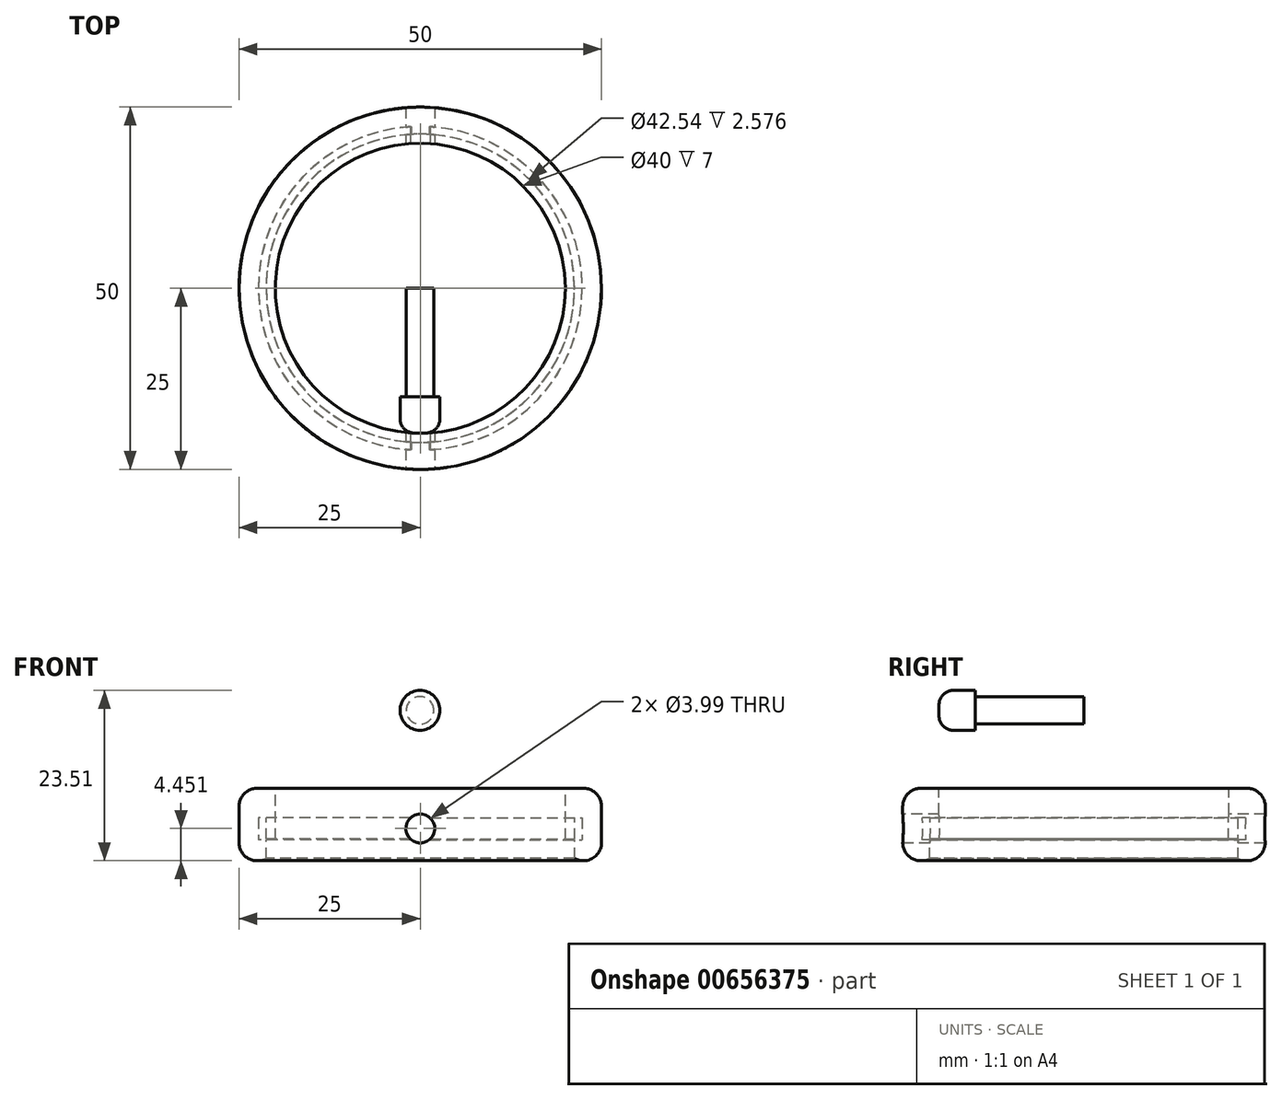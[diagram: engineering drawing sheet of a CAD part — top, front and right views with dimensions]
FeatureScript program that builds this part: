
annotation { "Feature Type Name" : "Feature", "Feature Type Description" : "" }
export const myFeature = defineFeature(function(context is Context, id is Id, definition is map)
    precondition{}
    {
        {
            var Q0;
            Q0=qCreatedBy(makeId("Top.planeOp"),FACE);
            var sketch = newSketch(context, id + "F0", { "sketchPlane" : qUnion([Q0])});
            skCircle(sketch, "E0", {"center": v(0, 0) * mm, "radius": 25 * mm});
            skSolve(sketch);
        }
        {
            var Q0;
            Q0 = qSketchRegion(id + "F0", true);
            extrude(context, id + "F1", {"entities" : qUnion([Q0]), "depth" : 10 * mm, "offsetDistance" : 25 * mm});
        }
        {
            var Q0;
            Q0=makeQuery(id+"F1.opExtrude","CAP_FACE",FACE,{"disambiguationData":[OSD([sQuery(id+"F0.wireOp",EDGE,"E0")])],"isStart":false});
            var sketch = newSketch(context, id + "F2", { "sketchPlane" : qUnion([Q0])});
            skCircle(sketch, "E1", {"center": v(0, 0) * mm, "radius": 20 * mm});
            skSolve(sketch);
        }
        {
            var Q0;
            Q0 = qSketchRegion(id + "F2", true);
            extrude(context, id + "F3", {"entities" : qUnion([Q0]), "operationType" : NewBodyOperationType.REMOVE, "oppositeDirection" : true, "depth" : 25 * mm, "offsetDistance" : 25 * mm});
        }
        {
            var Q0;
            Q0=makeQuery(id+"F1.opExtrude","CAP_EDGE",EDGE,{"disambiguationData":[OSD([sQuery(id+"F0.wireOp",EDGE,"E0")])],"isStart":false});
            var Q1;
            Q1=makeQuery(id+"F3.boolean.opBoolean","COPY",EDGE,{"derivedFrom":makeQuery(id+"F3.opExtrude","CAP_EDGE",EDGE,{"disambiguationData":[OSD([sQuery(id+"F2.wireOp",EDGE,"E1")])],"isStart":true})});
            var Q2;
            Q2=makeQuery(id+"F3.boolean.opBoolean","INTERSECT",EDGE,{"derivedFrom":[makeQuery(id+"F1.opExtrude","CAP_FACE",FACE,{"disambiguationData":[OSD([sQuery(id+"F0.wireOp",EDGE,"E0")])],"isStart":true}),makeQuery(id+"F3.opExtrude","SWEPT_FACE",FACE,{"disambiguationData":[OSD([sQuery(id+"F2.wireOp",EDGE,"E1")])]})]});
            var Q3;
            Q3=makeQuery(id+"F1.opExtrude","CAP_EDGE",EDGE,{"disambiguationData":[OSD([sQuery(id+"F0.wireOp",EDGE,"E0")])],"isStart":true});
            fillet(context, id + "F4", {"entities" : qUnion([Q0, Q1, Q2, Q3]), "radius" : 2.5 * mm, "tangentPropagation" : true, "allowEdgeOverflow" : false});
        }
        {
            var Q0;
            Q0=qCreatedBy(makeId("Top.planeOp"),FACE);
            var sketch = newSketch(context, id + "F5", { "sketchPlane" : qUnion([Q0])});
            skCircle(sketch, "E2", {"center": v(0, 0) * mm, "radius": 22.33 * mm});
            skSolve(sketch);
        }
        {
            var Q0;
            Q0 = qSketchRegion(id + "F5", true);
            extrude(context, id + "F6", {"entities" : qUnion([Q0]), "depth" : 3 * mm, "offsetDistance" : 25 * mm});
        }
        {
            var Q0;
            Q0=makeQuery(id+"F6.opExtrude","CAP_FACE",FACE,{"disambiguationData":[OSD([sQuery(id+"F5.wireOp",EDGE,"E2")])],"isStart":false});
            var sketch = newSketch(context, id + "F7", { "sketchPlane" : qUnion([Q0])});
            skCircle(sketch, "E3", {"center": v(0, 0) * mm, "radius": 21.27 * mm});
            skSolve(sketch);
        }
        {
            var Q0;
            Q0 = qSketchRegion(id + "F7", true);
            extrude(context, id + "F8", {"entities" : qUnion([Q0]), "operationType" : NewBodyOperationType.REMOVE, "oppositeDirection" : true, "depth" : 25 * mm, "offsetDistance" : 25 * mm});
        }
        {
            var Q0;
            Q0=makeQuery(id+"F6.opExtrude","SWEPT_BODY",BODY,{"disambiguationData":[OSD([sQuery(id+"F5.wireOp",EDGE,"E2")])]});
            transform(context, id + "F9", {"entities" : qUnion([Q0]), "transformType" : TransformType.TRANSLATION_3D, "dx" : 0 * mm, "dy" : 0 * mm, "dz" : 2.9 * mm, "makeCopy" : false});
        }
        {
            var Q0;
            Q0=makeQuery(id+"F6.opExtrude","SWEPT_BODY",BODY,{"disambiguationData":[OSD([sQuery(id+"F5.wireOp",EDGE,"E2")])]});
            var Q1;
            Q1=makeQuery(id+"F1.opExtrude","SWEPT_BODY",BODY,{"disambiguationData":[OSD([sQuery(id+"F0.wireOp",EDGE,"E0")])]});
            booleanBodies(context, id + "F10", {"operationType" : BooleanOperationType.SUBTRACTION, "tools" : qUnion([Q0]), "targets" : qUnion([Q1])});
        }
        {
            var Q0;
            Q0=qCreatedBy(makeId("Front.planeOp"),FACE);
            var sketch = newSketch(context, id + "F11", { "sketchPlane" : qUnion([Q0])});
            skCircle(sketch, "E4", {"center": v(0, 4.45) * mm, "radius": 2 * mm});
            skSolve(sketch);
        }
        {
            var Q0;
            Q0 = qSketchRegion(id + "F11", true);
            extrude(context, id + "F12", {"entities" : qUnion([Q0]), "operationType" : NewBodyOperationType.REMOVE, "oppositeDirection" : true, "depth" : 25 * mm, "offsetDistance" : 25 * mm, "hasSecondDirection" : true, "secondDirectionOppositeDirection" : false, "secondDirectionDepth" : 25 * mm});
        }
        {
            var Q0;
            Q0=qCreatedBy(makeId("Front.planeOp"),FACE);
            var sketch = newSketch(context, id + "F13", { "sketchPlane" : qUnion([Q0])});
            skCircle(sketch, "E5", {"center": v(-0.04, 4.46) * mm, "radius": 1.9 * mm});
            skPoint(sketch, "E5.first.point", {"position": v(0, 6.36) * mm});
            skPoint(sketch, "E5.second.point", {"position": v(0, 2.56) * mm});
            skPoint(sketch, "E5.third.point", {"position": v(1.86, 4.47) * mm});
            skSolve(sketch);
        }
        {
            var Q0;
            Q0 = qSketchRegion(id + "F13", true);
            extrude(context, id + "F14", {"entities" : qUnion([Q0]), "depth" : 15 * mm, "offsetDistance" : 25 * mm});
        }
        {
            var Q0;
            Q0=makeQuery(id+"F14.opExtrude","SWEPT_BODY",BODY,{"disambiguationData":[OSD([sQuery(id+"F13.wireOp",EDGE,"E5")])]});
            transform(context, id + "F15", {"entities" : qUnion([Q0]), "transformType" : TransformType.TRANSLATION_3D, "dx" : 0 * mm, "dy" : 0 * mm, "dz" : 16.3 * mm, "makeCopy" : false});
        }
        {
            var Q0;
            Q0=makeQuery(id+"F14.opExtrude","CAP_FACE",FACE,{"disambiguationData":[OSD([sQuery(id+"F13.wireOp",EDGE,"E5")])],"isStart":false});
            var sketch = newSketch(context, id + "F16", { "sketchPlane" : qUnion([Q0])});
            skCircle(sketch, "E6", {"center": v(-0.04, 20.76) * mm, "radius": 2.75 * mm});
            skSolve(sketch);
        }
        {
            var Q0;
            Q0 = qSketchRegion(id + "F16", true);
            extrude(context, id + "F17", {"entities" : qUnion([Q0]), "operationType" : NewBodyOperationType.ADD, "depth" : 5 * mm, "offsetDistance" : 25 * mm});
        }
        {
            var Q0;
            Q0=makeQuery(id+"F17.opExtrude","CAP_EDGE",EDGE,{"disambiguationData":[OSD([sQuery(id+"F16.wireOp",EDGE,"E6")])],"isStart":false});
            fillet(context, id + "F18", {"entities" : qUnion([Q0]), "radius" : 2 * mm, "tangentPropagation" : true, "allowEdgeOverflow" : false});
        }
    });
